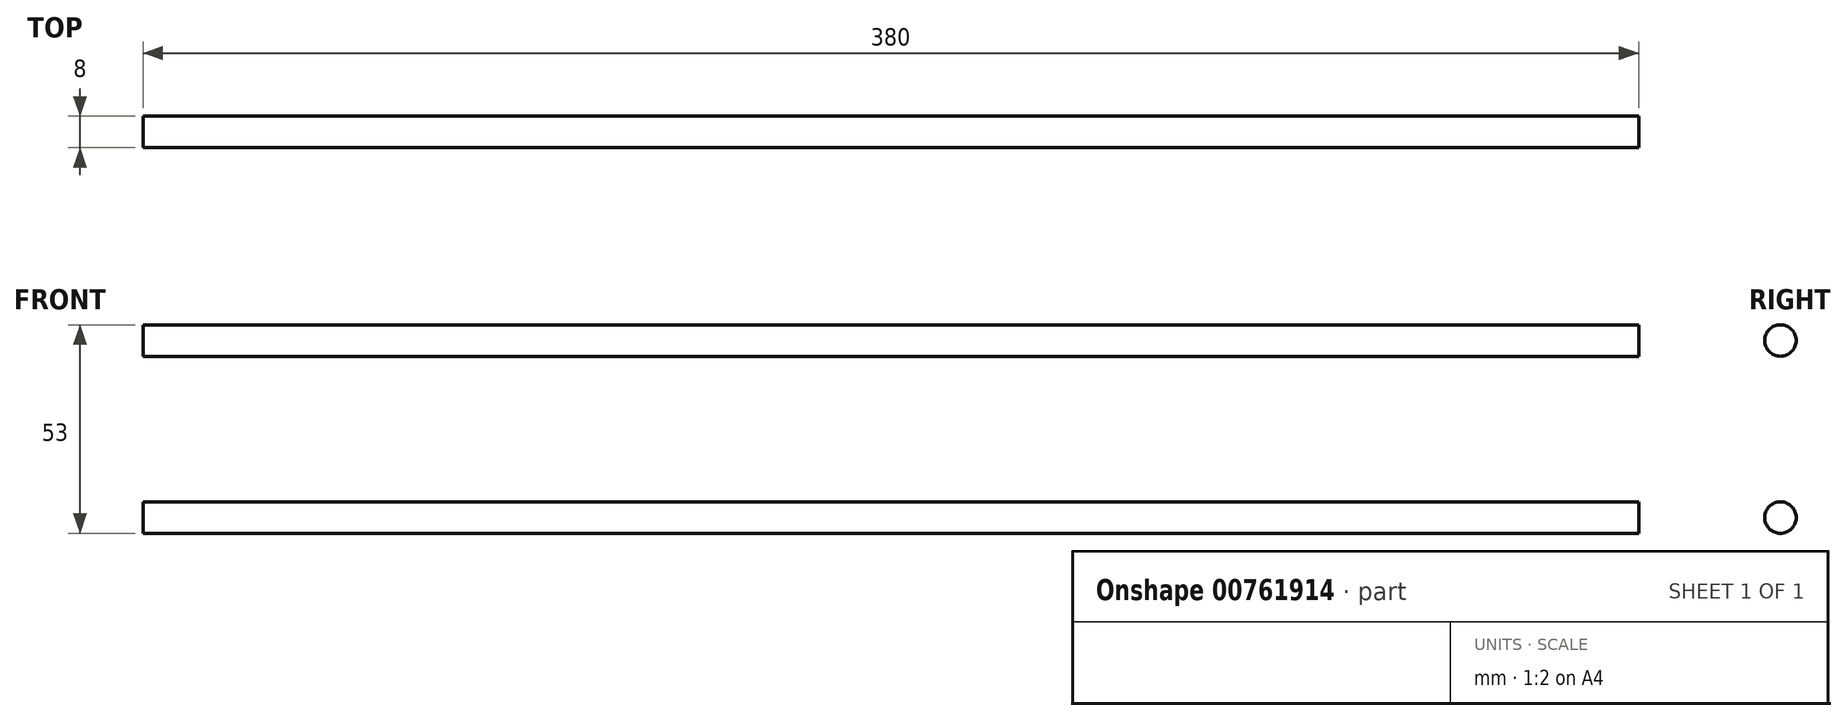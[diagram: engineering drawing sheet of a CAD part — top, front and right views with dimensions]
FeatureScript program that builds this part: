
annotation { "Feature Type Name" : "Feature", "Feature Type Description" : "" }
export const myFeature = defineFeature(function(context is Context, id is Id, definition is map)
    precondition{}
    {
        {
            var Q0;
            Q0=qCreatedBy(makeId("Right.planeOp"),FACE);
            var sketch = newSketch(context, id + "F0", { "sketchPlane" : qUnion([Q0])});
            skCircle(sketch, "E0", {"center": v(0, 22.5) * mm, "radius": 4 * mm});
            skCircle(sketch, "E1", {"center": v(0, -22.5) * mm, "radius": 4 * mm});
            skSolve(sketch);
        }
        {
            var Q0;
            Q0 = qSketchRegion(id + "F0", true);
            extrude(context, id + "F1", {"entities" : qUnion([Q0]), "depth" : 380 * mm, "offsetDistance" : 25 * mm});
        }
        {
            var Q0;
            Q0=makeQuery(id+"F1.opExtrude","SWEPT_BODY",BODY,{"disambiguationData":[OSD([sQuery(id+"F0.wireOp",EDGE,"E0")])]});
            var Q1;
            Q1=makeQuery(id+"F1.opExtrude","SWEPT_BODY",BODY,{"disambiguationData":[OSD([sQuery(id+"F0.wireOp",EDGE,"E1")])]});
            transform(context, id + "F2", {"entities" : qUnion([Q0, Q1]), "transformType" : TransformType.TRANSLATION_3D, "dx" : -380 / 2 * mm, "dy" : 0 * mm, "dz" : 0 * mm, "makeCopy" : false});
        }
    });
